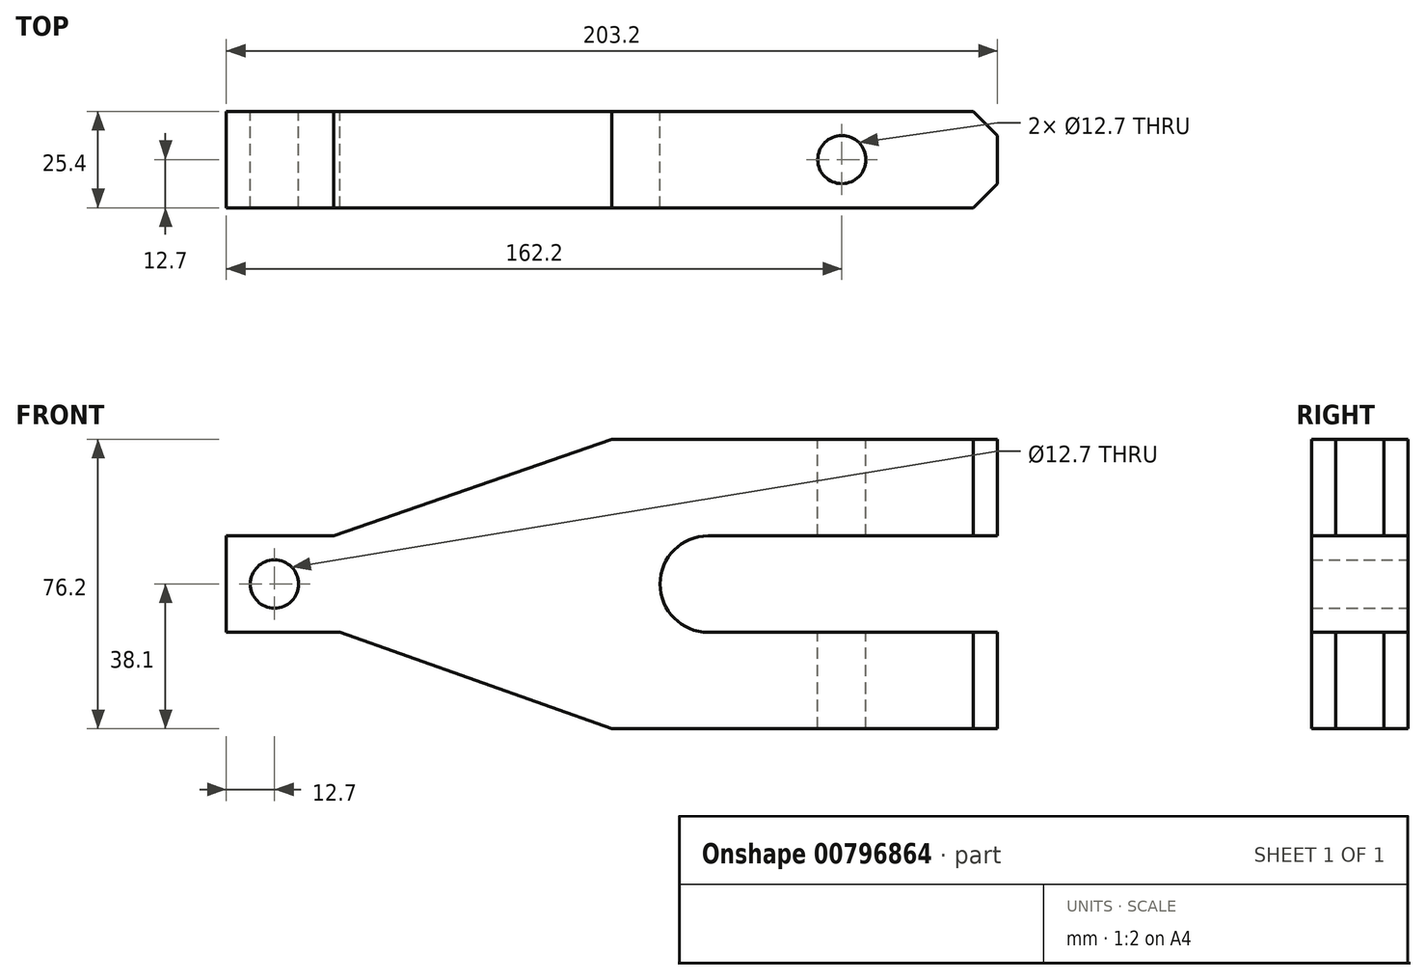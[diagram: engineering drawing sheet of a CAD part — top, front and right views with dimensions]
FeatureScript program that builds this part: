
annotation { "Feature Type Name" : "Feature", "Feature Type Description" : "" }
export const myFeature = defineFeature(function(context is Context, id is Id, definition is map)
    precondition{}
    {
        {
            var Q0;
            Q0=qCreatedBy(makeId("Front.planeOp"),FACE);
            var sketch = newSketch(context, id + "F0", { "sketchPlane" : qUnion([Q0])});
            skLineSegment(sketch, "E0", {"start": v(0, 0) * mm, "end": v(30, 0) * mm});
            skLineSegment(sketch, "E1", {"start": v(28.26, 25.4) * mm, "end": v(0, 25.4) * mm});
            skLineSegment(sketch, "E2", {"start": v(0, 25.4) * mm, "end": v(0, 0) * mm});
            skLineSegment(sketch, "E3", {"start": v(203.2, 50.8) * mm, "end": v(203.2, 25.4) * mm});
            skLineSegment(sketch, "E4", {"start": v(203.2, 25.4) * mm, "end": v(127, 25.4) * mm});
            skLineSegment(sketch, "E5", {"start": v(127, 0) * mm, "end": v(203.2, 0) * mm});
            skLineSegment(sketch, "E6", {"start": v(101.6, 50.8) * mm, "end": v(203.2, 50.8) * mm});
            skLineSegment(sketch, "E7", {"start": v(101.6, -25.4) * mm, "end": v(203.2, -25.4) * mm});
            skLineSegment(sketch, "E8", {"start": v(203.2, -25.4) * mm, "end": v(203.2, 0) * mm});
            skCircle(sketch, "E9", {"center": v(12.7, 12.7) * mm, "radius": 6.35 * mm});
            skArc(sketch, "E10.filletArc", {"start": v(127, 25.4) * mm, "mid": v(118.02, 21.68) * mm, "end": v(114.3, 12.7) * mm});
            skArc(sketch, "E11.filletArc", {"start": v(114.3, 12.7) * mm, "mid": v(118.02, 3.72) * mm, "end": v(127, 0) * mm});
            skLineSegment(sketch, "E12", {"start": v(114.3, 12.7) * mm, "end": v(114.3, 12.7) * mm});
            skLineSegment(sketch, "E13", {"start": v(101.6, 50.8) * mm, "end": v(28.26, 25.4) * mm});
            skLineSegment(sketch, "E14", {"start": v(101.6, -25.4) * mm, "end": v(30, 0) * mm});
            skSolve(sketch);
        }
        {
            var Q0;
            Q0=qCreatedBy(makeId("Top.planeOp"),FACE);
            var sketch = newSketch(context, id + "F1", { "sketchPlane" : qUnion([Q0])});
            skCircle(sketch, "E15", {"center": v(162.2, -12.7) * mm, "radius": 6.35 * mm});
            skSolve(sketch);
        }
        {
            var Q0;
            Q0=qSketchRegion(id+"F0",true);
            extrude(context, id + "F2", {"entities" : qUnion([Q0]), "depth" : 25.4 * mm, "offsetDistance" : 25.4 * mm});
        }
        {
            var Q0;
            Q0=makeQuery(id+"F2.opExtrude","CAP_EDGE",EDGE,{"disambiguationData":[OSD([sQuery(id+"F0.wireOp",EDGE,"E3")])],"isStart":false});
            var Q1;
            Q1=makeQuery(id+"F2.opExtrude","CAP_EDGE",EDGE,{"disambiguationData":[OSD([sQuery(id+"F0.wireOp",EDGE,"E8")])],"isStart":false});
            var Q2;
            Q2=makeQuery(id+"F2.opExtrude","CAP_EDGE",EDGE,{"disambiguationData":[OSD([sQuery(id+"F0.wireOp",EDGE,"E8")])],"isStart":true});
            var Q3;
            Q3=makeQuery(id+"F2.opExtrude","CAP_EDGE",EDGE,{"disambiguationData":[OSD([sQuery(id+"F0.wireOp",EDGE,"E3")])],"isStart":true});
            chamfer(context, id + "F3", {"entities" : qUnion([Q0, Q1, Q2, Q3]), "chamferType" : ChamferType.OFFSET_ANGLE, "width" : 6.35 * mm, "oppositeDirection" : false, "angle" : 45 * degree, "tangentPropagation" : true});
        }
        {
            var Q0;
            Q0=qSketchRegion(id+"F1",true);
            extrude(context, id + "F4", {"entities" : qUnion([Q0]), "operationType" : NewBodyOperationType.REMOVE, "endBound" : BoundingType.SYMMETRIC, "oppositeDirection" : true, "depth" : 254 * mm, "offsetDistance" : 25.4 * mm});
        }
    });
